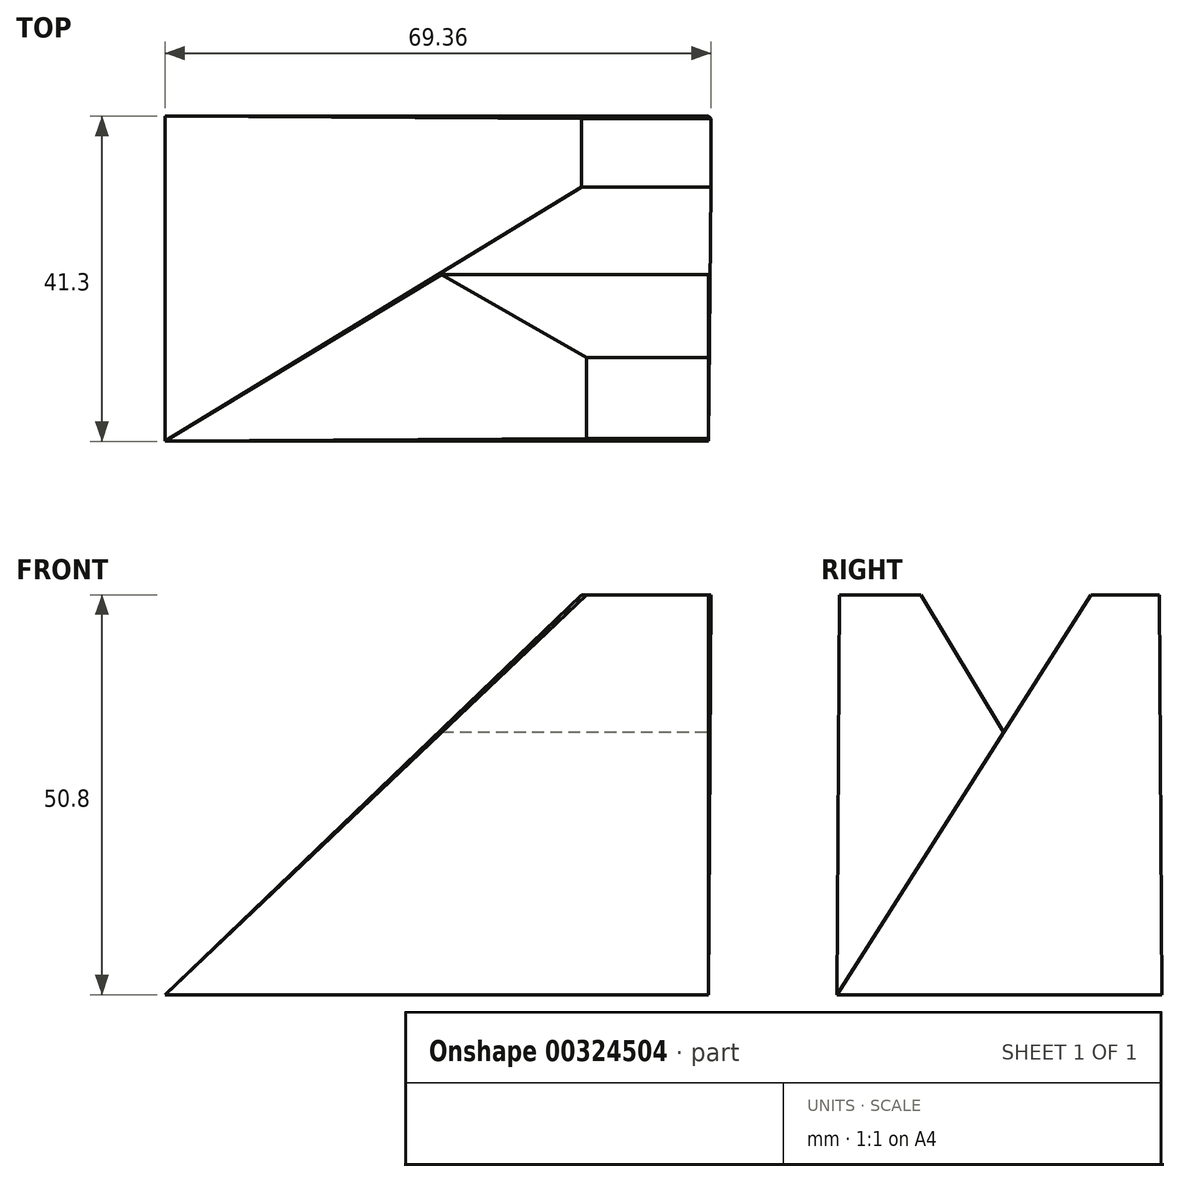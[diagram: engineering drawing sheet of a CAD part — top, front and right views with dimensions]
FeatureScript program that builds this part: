
annotation { "Feature Type Name" : "Feature", "Feature Type Description" : "" }
export const myFeature = defineFeature(function(context is Context, id is Id, definition is map)
    precondition{}
    {
        {
            var Q0;
            Q0=qCreatedBy(makeId("Top.planeOp"),FACE);
            var sketch = newSketch(context, id + "F0", { "sketchPlane" : qUnion([Q0])});
            skLineSegment(sketch, "E0.bottom", {"start": v(34.52, 20.65) * mm, "end": v(-34.52, 20.65) * mm});
            skLineSegment(sketch, "E0.top", {"start": v(34.52, -20.65) * mm, "end": v(-34.52, -20.65) * mm});
            skLineSegment(sketch, "E0.left", {"start": v(34.52, 20.65) * mm, "end": v(34.52, -20.65) * mm});
            skLineSegment(sketch, "E0.right", {"start": v(-34.52, 20.65) * mm, "end": v(-34.52, -20.65) * mm});
            skPoint(sketch, "E0.middle", {"position": v(0, 0) * mm});
            skLineSegment(sketch, "E1.bottom", {"start": v(-34.52, 20.65) * mm, "end": v(-20.97, 20.65) * mm});
            skLineSegment(sketch, "E1.left", {"start": v(-34.52, 20.65) * mm, "end": v(-34.52, 12.9) * mm});
            skLineSegment(sketch, "E2.bottom", {"start": v(34.52, 20.65) * mm, "end": v(19.03, 20.65) * mm});
            skLineSegment(sketch, "E2.left", {"start": v(34.52, 20.65) * mm, "end": v(34.52, 11.61) * mm});
            skLineSegment(sketch, "E3.bottom", {"start": v(-34.52, -20.65) * mm, "end": v(-20.33, -20.65) * mm});
            skLineSegment(sketch, "E3.left", {"start": v(-34.52, -20.65) * mm, "end": v(-34.52, -11.61) * mm});
            skSolve(sketch);
        }
        {
            var Q0;
            Q0=qCreatedBy(makeId("Top.planeOp"),FACE);
            cPlane(context, id + "F1", {"entities" : qUnion([Q0]), "cplaneType" : CPlaneType.OFFSET, "offset" : 50.8 * mm, "width" : 152.4 * mm, "height" : 152.4 * mm});
        }
        {
            var Q0;
            Q0=qCreatedBy(id+"F1.planeOp",FACE);
            var sketch = newSketch(context, id + "F2", { "sketchPlane" : qUnion([Q0])});
            skLineSegment(sketch, "E4.bottom", {"start": v(-34.52, 20.33) * mm, "end": v(-20.65, 20.33) * mm});
            skLineSegment(sketch, "E4.top", {"start": v(-34.52, 12.9) * mm, "end": v(-20.65, 12.9) * mm});
            skLineSegment(sketch, "E4.left", {"start": v(-34.52, 20.33) * mm, "end": v(-34.52, 12.9) * mm});
            skLineSegment(sketch, "E4.right", {"start": v(-20.65, 20.33) * mm, "end": v(-20.65, 12.9) * mm});
            skLineSegment(sketch, "E5.bottom", {"start": v(34.84, 20.33) * mm, "end": v(18.39, 20.33) * mm});
            skLineSegment(sketch, "E5.top", {"start": v(34.84, 11.61) * mm, "end": v(18.39, 11.61) * mm});
            skLineSegment(sketch, "E5.left", {"start": v(34.84, 20.33) * mm, "end": v(34.84, 11.61) * mm});
            skLineSegment(sketch, "E5.right", {"start": v(18.39, 20.33) * mm, "end": v(18.39, 11.61) * mm});
            skLineSegment(sketch, "E6.bottom", {"start": v(-33.55, -20) * mm, "end": v(-20, -20) * mm});
            skLineSegment(sketch, "E6.top", {"start": v(-33.55, -11.61) * mm, "end": v(-20, -11.61) * mm});
            skLineSegment(sketch, "E6.left", {"start": v(-33.55, -20) * mm, "end": v(-33.55, -11.61) * mm});
            skLineSegment(sketch, "E6.right", {"start": v(-20, -20) * mm, "end": v(-20, -11.61) * mm});
            skLineSegment(sketch, "E7.bottom", {"start": v(34.52, -20.33) * mm, "end": v(19.03, -20.33) * mm});
            skLineSegment(sketch, "E7.top", {"start": v(34.52, -10) * mm, "end": v(19.03, -10) * mm});
            skLineSegment(sketch, "E7.left", {"start": v(34.52, -20.33) * mm, "end": v(34.52, -10) * mm});
            skLineSegment(sketch, "E7.right", {"start": v(19.03, -20.33) * mm, "end": v(19.03, -10) * mm});
            skSolve(sketch);
        }
        {
            var Q0;
            Q0=makeQuery(id+"F0.imprint","IMPRINT",FACE,{"disambiguationData":[TD([[makeQuery(id+"F0.imprint","IMPRINT",EDGE,{"derivedFrom":sQuery(id+"F0.wireOp",EDGE,"E0.bottom")}),1.0]])]});
            var Q1;
            Q1=makeQuery(id+"F2.imprint","IMPRINT",FACE,{"disambiguationData":[TD([[makeQuery(id+"F2.imprint","IMPRINT",EDGE,{"derivedFrom":sQuery(id+"F2.wireOp",EDGE,"E5.bottom")}),1.0]])]});
            loft(context, id + "F3", {"sheetProfilesArray" : [{ "sheetProfileEntities" : qUnion([Q0]) }, { "sheetProfileEntities" : qUnion([Q1]) }]});
        }
        {
            var Q1;
            Q1=makeQuery(id+"F3.opLoft","CAP_FACE",FACE,{"disambiguationData":[OSD([makeQuery(id+"F0.imprint","IMPRINT",FACE,{"disambiguationData":[TD([[makeQuery(id+"F0.imprint","IMPRINT",EDGE,{"derivedFrom":sQuery(id+"F0.wireOp",EDGE,"E0.bottom")}),1.0]])]})])],"isStart":true});
            var Q2;
            Q2=makeQuery(id+"F2.imprint","IMPRINT",FACE,{"disambiguationData":[TD([[makeQuery(id+"F2.imprint","IMPRINT",EDGE,{"derivedFrom":sQuery(id+"F2.wireOp",EDGE,"E7.bottom")}),-1.0]])]});
            loft(context, id + "F4", {"operationType" : NewBodyOperationType.ADD, "sheetProfilesArray" : [{ "sheetProfileEntities" : qUnion([Q1]) }, { "sheetProfileEntities" : qUnion([Q2]) }]});
        }
    });
